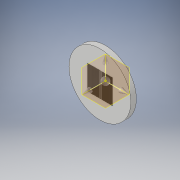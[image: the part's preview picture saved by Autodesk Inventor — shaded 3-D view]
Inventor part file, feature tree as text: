
AUTODESK INVENTOR PART (.ipt)
format: ipt  version: 2018 (Build 220112000, 112)  size: 297,984 bytes
history: native  units: in
note: dims shown in document units (in); Inventor stores cm internally (conversion verified against a paired STEP export)
features: extrude x1, sketch x1
ambient origin geometry x8: Origin, YZ Plane, XZ Plane, XY Plane, X Axis, Y Axis, Z Axis, Center Point
bodies: Body1 (feature_tree)
feature tree (2):
  extrude  "Extrusion2"  Depth=0.09in
  sketch  "Sketch9"  dims[d4=0.09in d5=0.0in d3=1.0in]
